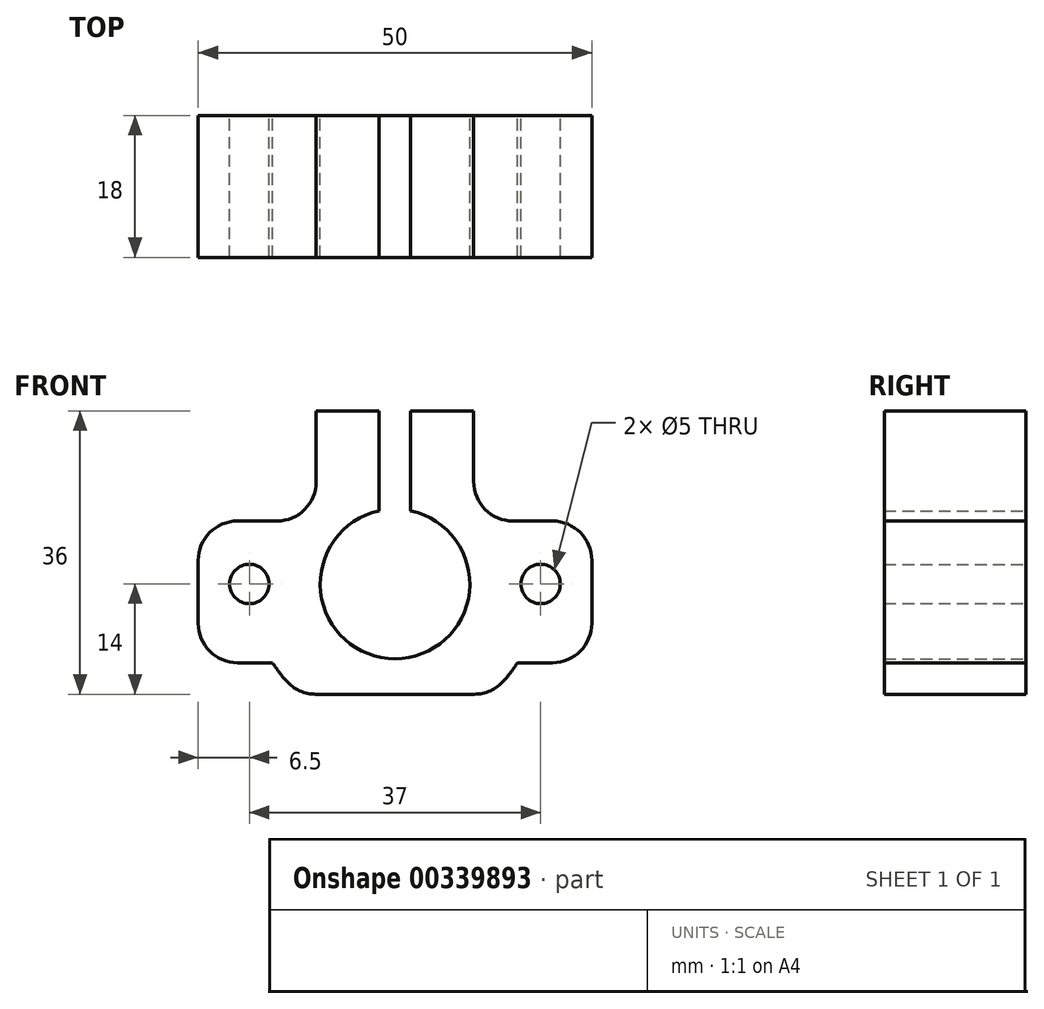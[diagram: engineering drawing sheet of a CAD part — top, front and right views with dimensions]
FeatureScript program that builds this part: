
annotation { "Feature Type Name" : "Feature", "Feature Type Description" : "" }
export const myFeature = defineFeature(function(context is Context, id is Id, definition is map)
    precondition{}
    {
        {
            var Q0;
            Q0=qCreatedBy(makeId("Front.planeOp"),FACE);
            var sketch = newSketch(context, id + "F0", { "sketchPlane" : qUnion([Q0])});
            skCircle(sketch, "E0", {"center": v(0, 0) * mm, "radius": 9.5 * mm});
            skCircle(sketch, "E1", {"center": v(0, 0) * mm, "radius": 18.5 * mm});
            skLineSegment(sketch, "E2.bottom", {"start": v(-25, 8) * mm, "end": v(25, 8) * mm});
            skLineSegment(sketch, "E2.top", {"start": v(-25, -10) * mm, "end": v(25, -10) * mm});
            skLineSegment(sketch, "E2.left", {"start": v(-25, 8) * mm, "end": v(-25, -10) * mm});
            skLineSegment(sketch, "E2.right", {"start": v(25, 8) * mm, "end": v(25, -10) * mm});
            skLineSegment(sketch, "E3.bottom", {"start": v(-10, 22) * mm, "end": v(10, 22) * mm});
            skLineSegment(sketch, "E3.top", {"start": v(-10, 0) * mm, "end": v(10, 0) * mm});
            skLineSegment(sketch, "E3.left", {"start": v(-10, 22) * mm, "end": v(-10, 0) * mm});
            skLineSegment(sketch, "E3.right", {"start": v(10, 22) * mm, "end": v(10, 0) * mm});
            skLineSegment(sketch, "E4.bottom", {"start": v(-2, 32.08) * mm, "end": v(2, 32.08) * mm});
            skLineSegment(sketch, "E4.top", {"start": v(-2, 0) * mm, "end": v(2, 0) * mm});
            skLineSegment(sketch, "E4.left", {"start": v(-2, 32.08) * mm, "end": v(-2, 0) * mm});
            skLineSegment(sketch, "E4.right", {"start": v(2, 32.08) * mm, "end": v(2, 0) * mm});
            skCircle(sketch, "E5", {"center": v(-18.5, 0) * mm, "radius": 2.5 * mm});
            skCircle(sketch, "E6", {"center": v(18.5, 0) * mm, "radius": 2.5 * mm});
            skLineSegment(sketch, "E7", {"start": v(-12.1, -14) * mm, "end": v(12.1, -14) * mm});
            skSolve(sketch);
        }
        {
            var Q0;
            {var subQ0=sQuery(id+"F0.wireOp",EDGE,"E2.top");var subQ1=sQuery(id+"F0.wireOp",EDGE,"E1");var subQ2=makeQuery(id+"F0.imprint","INTERSECT",VERTEX,{"disambiguationData":[OD(0.0)],"derivedFrom":[subQ1,subQ0]});Q0=makeQuery(id+"F0.imprint","IMPRINT",FACE,{"disambiguationData":[TD([[makeQuery(id+"F0.imprint","IMPRINT",EDGE,{"disambiguationData":[TD([[subQ2,-1.0]])],"derivedFrom":subQ1}),1.0]])]});}
            var Q1;
            {var subQ0=sQuery(id+"F0.wireOp",EDGE,"E2.right");Q1=makeQuery(id+"F0.imprint","IMPRINT",FACE,{"disambiguationData":[TD([[makeQuery(id+"F0.imprint","IMPRINT",EDGE,{"derivedFrom":subQ0}),-1.0]])]});}
            var Q2;
            {var subQ0=sQuery(id+"F0.wireOp",EDGE,"E3.right");var subQ1=sQuery(id+"F0.wireOp",EDGE,"E1");var subQ2=makeQuery(id+"F0.imprint","INTERSECT",VERTEX,{"derivedFrom":[subQ1,subQ0]});Q2=makeQuery(id+"F0.imprint","IMPRINT",FACE,{"disambiguationData":[TD([[makeQuery(id+"F0.imprint","IMPRINT",EDGE,{"disambiguationData":[TD([[subQ2,-1.0]])],"derivedFrom":subQ1}),-1.0]])]});}
            var Q3;
            {var subQ0=sQuery(id+"F0.wireOp",EDGE,"E3.left");var subQ1=sQuery(id+"F0.wireOp",EDGE,"E1");var subQ2=makeQuery(id+"F0.imprint","INTERSECT",VERTEX,{"derivedFrom":[subQ1,subQ0]});Q3=makeQuery(id+"F0.imprint","IMPRINT",FACE,{"disambiguationData":[TD([[makeQuery(id+"F0.imprint","IMPRINT",EDGE,{"disambiguationData":[TD([[subQ2,1.0]])],"derivedFrom":subQ1}),-1.0]])]});}
            var Q4;
            {var subQ0=sQuery(id+"F0.wireOp",EDGE,"E2.left");Q4=makeQuery(id+"F0.imprint","IMPRINT",FACE,{"disambiguationData":[TD([[makeQuery(id+"F0.imprint","IMPRINT",EDGE,{"derivedFrom":subQ0}),1.0]])]});}
            var Q5;
            {var subQ0=sQuery(id+"F0.wireOp",EDGE,"E2.bottom");var subQ1=sQuery(id+"F0.wireOp",EDGE,"E0");var subQ2=makeQuery(id+"F0.imprint","INTERSECT",VERTEX,{"disambiguationData":[OD(0.0)],"derivedFrom":[subQ1,subQ0]});Q5=makeQuery(id+"F0.imprint","IMPRINT",FACE,{"disambiguationData":[TD([[makeQuery(id+"F0.imprint","IMPRINT",EDGE,{"disambiguationData":[TD([[subQ2,-1.0]])],"derivedFrom":subQ1}),-1.0]])]});}
            var Q6;
            {var subQ5=sQuery(id+"F0.wireOp",EDGE,"E0");var subQ7=sQuery(id+"F0.wireOp",EDGE,"E4.left");var subQ9=makeQuery(id+"F0.imprint","INTERSECT",VERTEX,{"derivedFrom":[subQ5,subQ7]});Q6=makeQuery(id+"F0.imprint","IMPRINT",FACE,{"disambiguationData":[TD([[makeQuery(id+"F0.imprint","IMPRINT",EDGE,{"disambiguationData":[TD([[subQ9,-1.0]])],"derivedFrom":subQ5}),-1.0]])]});}
            var Q7;
            {var subQ1=sQuery(id+"F0.wireOp",EDGE,"E3.top");var subQ3=sQuery(id+"F0.wireOp",EDGE,"E0");var subQ14=makeQuery(id+"F0.imprint","INTERSECT",VERTEX,{"disambiguationData":[OD(0.0)],"derivedFrom":[subQ3,subQ1]});Q7=makeQuery(id+"F0.imprint","IMPRINT",FACE,{"disambiguationData":[TD([[makeQuery(id+"F0.imprint","IMPRINT",EDGE,{"disambiguationData":[TD([[subQ14,1.0]])],"derivedFrom":subQ3}),-1.0]])]});}
            var Q8;
            {var subQ0=sQuery(id+"F0.wireOp",EDGE,"E2.bottom");var subQ1=sQuery(id+"F0.wireOp",EDGE,"E0");var subQ2=makeQuery(id+"F0.imprint","INTERSECT",VERTEX,{"disambiguationData":[OD(1.0)],"derivedFrom":[subQ1,subQ0]});Q8=makeQuery(id+"F0.imprint","IMPRINT",FACE,{"disambiguationData":[TD([[makeQuery(id+"F0.imprint","IMPRINT",EDGE,{"disambiguationData":[TD([[subQ2,-1.0]])],"derivedFrom":subQ1}),-1.0]])]});}
            var Q9;
            {var subQ0=sQuery(id+"F0.wireOp",EDGE,"E2.bottom");var subQ1=sQuery(id+"F0.wireOp",EDGE,"E0");var subQ2=makeQuery(id+"F0.imprint","INTERSECT",VERTEX,{"disambiguationData":[OD(0.0)],"derivedFrom":[subQ1,subQ0]});Q9=makeQuery(id+"F0.imprint","IMPRINT",FACE,{"disambiguationData":[TD([[makeQuery(id+"F0.imprint","IMPRINT",EDGE,{"disambiguationData":[TD([[subQ2,1.0]])],"derivedFrom":subQ1}),-1.0]])]});}
            extrude(context, id + "F1", {"entities" : qUnion([Q0, Q1, Q2, Q3, Q4, Q5, Q6, Q7, Q8, Q9]), "depth" : 18 * mm});
        }
        {
            var Q0;
            Q0=makeQuery(id+"F1.opExtrude","SWEPT_EDGE",EDGE,{"disambiguationData":[OSD([sQuery(id+"F0.wireOp",EDGE,"E2.bottom"),sQuery(id+"F0.wireOp",EDGE,"E2.left")])]});
            var Q1;
            Q1=makeQuery(id+"F1.opExtrude","SWEPT_EDGE",EDGE,{"disambiguationData":[OSD([sQuery(id+"F0.wireOp",EDGE,"E2.top"),sQuery(id+"F0.wireOp",EDGE,"E2.left")])]});
            var Q2;
            Q2=makeQuery(id+"F1.opExtrude","SWEPT_EDGE",EDGE,{"disambiguationData":[OSD([sQuery(id+"F0.wireOp",EDGE,"E2.top"),sQuery(id+"F0.wireOp",EDGE,"E2.right")])]});
            var Q3;
            Q3=makeQuery(id+"F1.opExtrude","SWEPT_EDGE",EDGE,{"disambiguationData":[OSD([sQuery(id+"F0.wireOp",EDGE,"E2.bottom"),sQuery(id+"F0.wireOp",EDGE,"E2.right")])]});
            var Q4;
            Q4=makeQuery(id+"F1.opExtrude","SWEPT_EDGE",EDGE,{"disambiguationData":[OSD([sQuery(id+"F0.wireOp",EDGE,"E2.bottom"),sQuery(id+"F0.wireOp",EDGE,"E3.right")])]});
            var Q5;
            Q5=makeQuery(id+"F1.opExtrude","SWEPT_EDGE",EDGE,{"disambiguationData":[OSD([sQuery(id+"F0.wireOp",EDGE,"E2.bottom"),sQuery(id+"F0.wireOp",EDGE,"E3.left")])]});
            var Q6;
            {var subQ0=sQuery(id+"F0.wireOp",EDGE,"E7");var subQ1=sQuery(id+"F0.wireOp",EDGE,"E1");Q6=makeQuery(id+"F1.opExtrude","SWEPT_EDGE",EDGE,{"disambiguationData":[OSD([subQ1,subQ0]),TDD([makeQuery(id+"F0.imprint","INTERSECT",VERTEX,{"disambiguationData":[OD(0.0)],"derivedFrom":[subQ1,subQ0]})])]});}
            var Q7;
            {var subQ0=sQuery(id+"F0.wireOp",EDGE,"E7");var subQ1=sQuery(id+"F0.wireOp",EDGE,"E1");Q7=makeQuery(id+"F1.opExtrude","SWEPT_EDGE",EDGE,{"disambiguationData":[OSD([subQ1,subQ0]),TDD([makeQuery(id+"F0.imprint","INTERSECT",VERTEX,{"disambiguationData":[OD(1.0)],"derivedFrom":[subQ1,subQ0]})])]});}
            fillet(context, id + "F2", {"entities" : qUnion([Q0, Q1, Q2, Q3, Q4, Q5, Q6, Q7]), "radius" : 5 * mm, "tangentPropagation" : true, "allowEdgeOverflow" : false});
        }
    });
